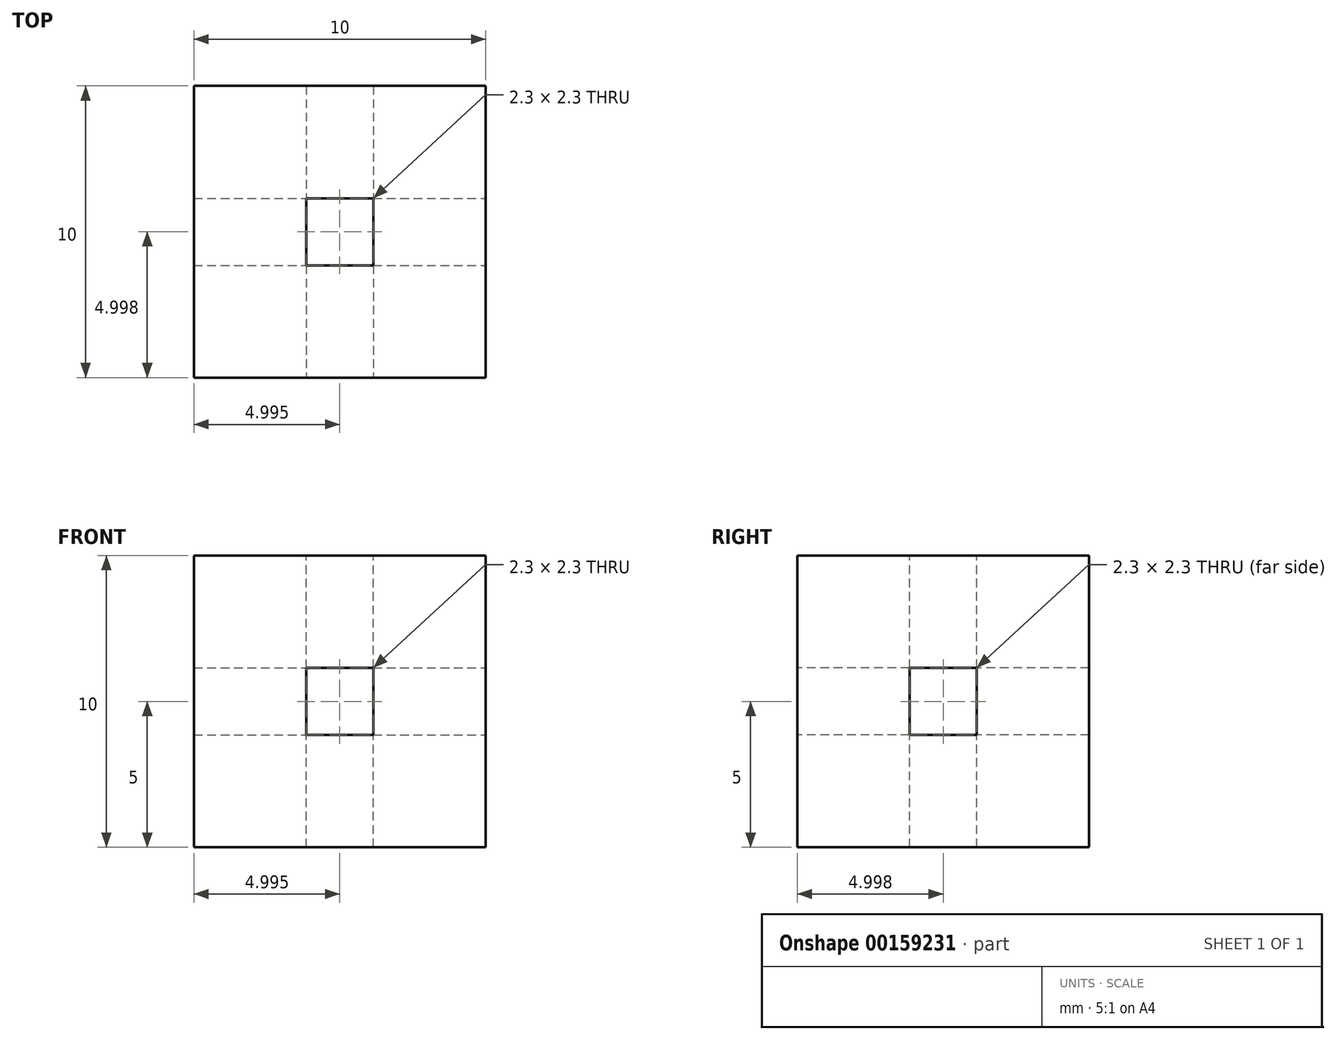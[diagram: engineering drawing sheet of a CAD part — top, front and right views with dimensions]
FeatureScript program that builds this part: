
annotation { "Feature Type Name" : "Feature", "Feature Type Description" : "" }
export const myFeature = defineFeature(function(context is Context, id is Id, definition is map)
    precondition{}
    {
        {
            var Q0;
            Q0=qCreatedBy(makeId("Top.planeOp"),FACE);
            var sketch = newSketch(context, id + "F0", { "sketchPlane" : qUnion([Q0])});
            skLineSegment(sketch, "E0.bottom", {"start": v(-12.52, 12.2) * mm, "end": v(-2.52, 12.2) * mm});
            skLineSegment(sketch, "E0.top", {"start": v(-12.52, 2.2) * mm, "end": v(-2.52, 2.2) * mm});
            skLineSegment(sketch, "E0.left", {"start": v(-12.52, 12.2) * mm, "end": v(-12.52, 2.2) * mm});
            skLineSegment(sketch, "E0.right", {"start": v(-2.52, 12.2) * mm, "end": v(-2.52, 2.2) * mm});
            skSolve(sketch);
        }
        {
            var Q0;
            Q0=qSketchRegion(id+"F0",true);
            extrude(context, id + "F1", {"entities" : qUnion([Q0]), "depth" : 10 * mm});
        }
        {
            var Q0;
            Q0=makeQuery(id+"F1.opExtrude","CAP_FACE",FACE,{"disambiguationData":[OSD([sQuery(id+"F0.wireOp",EDGE,"E0.bottom"),sQuery(id+"F0.wireOp",EDGE,"E0.top"),sQuery(id+"F0.wireOp",EDGE,"E0.left"),sQuery(id+"F0.wireOp",EDGE,"E0.right")])],"isStart":false});
            var sketch = newSketch(context, id + "F2", { "sketchPlane" : qUnion([Q0])});
            skLineSegment(sketch, "E1", {"start": v(-12.52, 7.2) * mm, "end": v(-2.52, 7.2) * mm, "construction": true});
            skLineSegment(sketch, "E2", {"start": v(-7.52, 2.2) * mm, "end": v(-7.52, 12.2) * mm, "construction": true});
            skLineSegment(sketch, "E3.bottom", {"start": v(-6.37, 6.06) * mm, "end": v(-8.67, 6.06) * mm});
            skLineSegment(sketch, "E3.top", {"start": v(-6.37, 8.36) * mm, "end": v(-8.67, 8.36) * mm});
            skLineSegment(sketch, "E3.left", {"start": v(-6.37, 6.06) * mm, "end": v(-6.37, 8.36) * mm});
            skLineSegment(sketch, "E3.right", {"start": v(-8.67, 6.06) * mm, "end": v(-8.67, 8.36) * mm});
            skPoint(sketch, "E3.middle", {"position": v(-7.52, 7.2) * mm});
            skSolve(sketch);
        }
        {
            var Q0;
            Q0=makeQuery(id+"F1.opExtrude","SWEPT_FACE",FACE,{"disambiguationData":[OSD([sQuery(id+"F0.wireOp",EDGE,"E0.top")])]});
            var sketch = newSketch(context, id + "F3", { "sketchPlane" : qUnion([Q0])});
            skLineSegment(sketch, "E4", {"start": v(-7.52, 10) * mm, "end": v(-7.52, 0) * mm, "construction": true});
            skLineSegment(sketch, "E5.bottom", {"start": v(-6.37, 6.15) * mm, "end": v(-8.67, 6.15) * mm});
            skLineSegment(sketch, "E5.top", {"start": v(-6.37, 3.85) * mm, "end": v(-8.67, 3.85) * mm});
            skLineSegment(sketch, "E5.left", {"start": v(-6.37, 6.15) * mm, "end": v(-6.37, 3.85) * mm});
            skLineSegment(sketch, "E5.right", {"start": v(-8.67, 6.15) * mm, "end": v(-8.67, 3.85) * mm});
            skPoint(sketch, "E5.middle", {"position": v(-7.52, 5) * mm});
            skSolve(sketch);
        }
        {
            var Q0;
            Q0=makeQuery(id+"F1.opExtrude","SWEPT_FACE",FACE,{"disambiguationData":[OSD([sQuery(id+"F0.wireOp",EDGE,"E0.right")])]});
            var sketch = newSketch(context, id + "F4", { "sketchPlane" : qUnion([Q0])});
            skLineSegment(sketch, "E6", {"start": v(7.2, 10) * mm, "end": v(7.2, 0) * mm, "construction": true});
            skLineSegment(sketch, "E7.bottom", {"start": v(8.36, 6.15) * mm, "end": v(6.06, 6.15) * mm});
            skLineSegment(sketch, "E7.top", {"start": v(8.36, 3.85) * mm, "end": v(6.06, 3.85) * mm});
            skLineSegment(sketch, "E7.left", {"start": v(8.36, 6.15) * mm, "end": v(8.36, 3.85) * mm});
            skLineSegment(sketch, "E7.right", {"start": v(6.06, 6.15) * mm, "end": v(6.06, 3.85) * mm});
            skPoint(sketch, "E7.middle", {"position": v(7.2, 5) * mm});
            skSolve(sketch);
        }
        {
            var Q0;
            Q0 = qSketchRegion(id + "F2", true);
            extrude(context, id + "F5", {"entities" : qUnion([Q0]), "operationType" : NewBodyOperationType.REMOVE, "endBound" : BoundingType.THROUGH_ALL, "oppositeDirection" : true, "depth" : 25 * mm});
        }
        {
            var Q0;
            Q0 = qSketchRegion(id + "F3", true);
            extrude(context, id + "F6", {"entities" : qUnion([Q0]), "operationType" : NewBodyOperationType.REMOVE, "endBound" : BoundingType.THROUGH_ALL, "oppositeDirection" : true, "depth" : 25 * mm});
        }
        {
            var Q0;
            Q0 = qSketchRegion(id + "F4", true);
            extrude(context, id + "F7", {"entities" : qUnion([Q0]), "operationType" : NewBodyOperationType.REMOVE, "endBound" : BoundingType.THROUGH_ALL, "oppositeDirection" : true, "depth" : 25 * mm});
        }
    });
